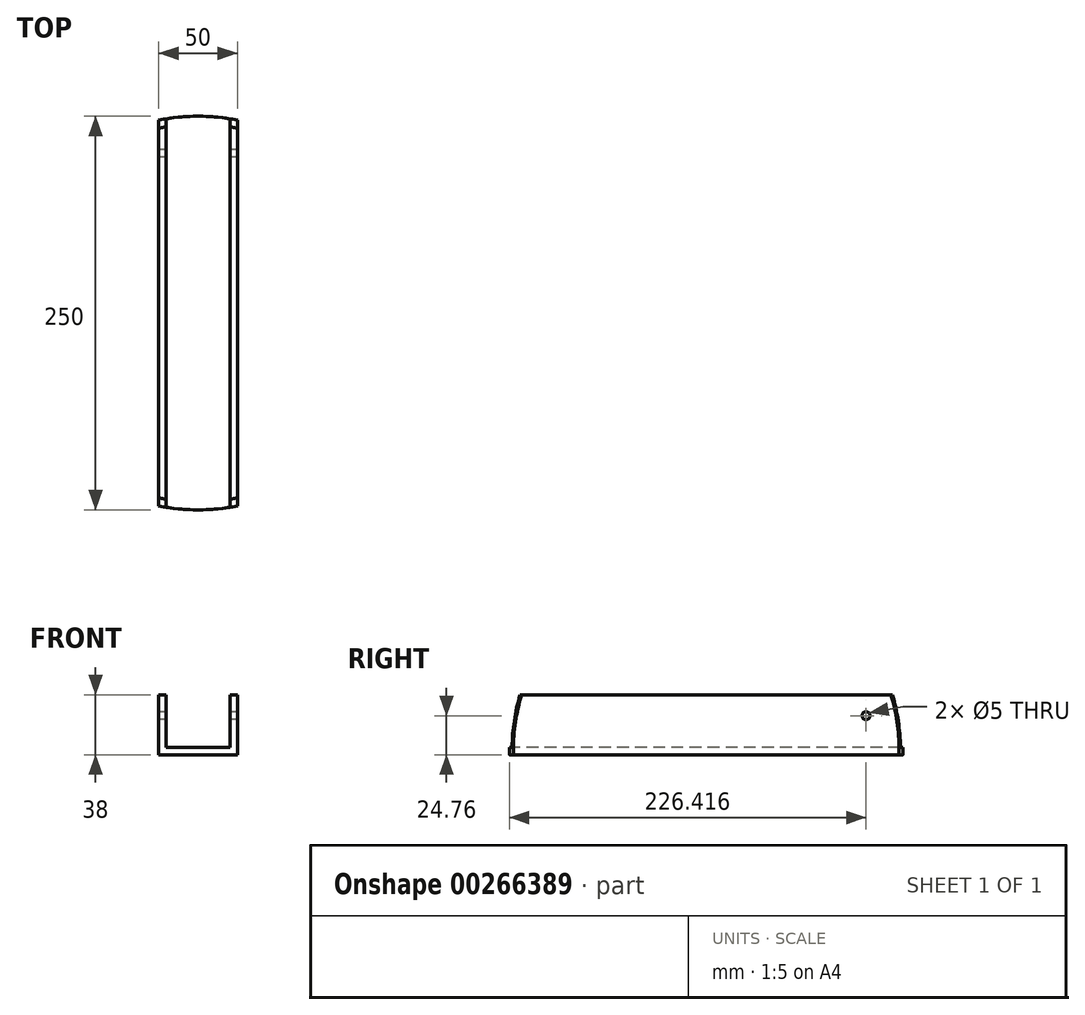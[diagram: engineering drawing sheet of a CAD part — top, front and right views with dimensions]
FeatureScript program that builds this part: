
annotation { "Feature Type Name" : "Feature", "Feature Type Description" : "" }
export const myFeature = defineFeature(function(context is Context, id is Id, definition is map)
    precondition{}
    {
        {
            var Q0;
            Q0=qCreatedBy(makeId("Top.planeOp"),FACE);
            var sketch = newSketch(context, id + "F0", { "sketchPlane" : qUnion([Q0])});
            skCircle(sketch, "E0", {"center": v(0, 0) * mm, "radius": 125 * mm});
            skLineSegment(sketch, "E1", {"start": v(0, 0) * mm, "end": v(0, 125) * mm});
            skLineSegment(sketch, "E2", {"start": v(0, 0) * mm, "end": v(0, -125) * mm});
            skLineSegment(sketch, "E3", {"start": v(0, 0) * mm, "end": v(-25, 0) * mm, "construction": true});
            skLineSegment(sketch, "E4", {"start": v(0, 0) * mm, "end": v(25, 0) * mm, "construction": true});
            skCircle(sketch, "E5", {"center": v(0, 0) * mm, "radius": 122 * mm});
            skLineSegment(sketch, "E6", {"start": v(-25, 90.35) * mm, "end": v(-25, 119.41) * mm});
            skLineSegment(sketch, "E7", {"start": v(25, 90.35) * mm, "end": v(25, 119.41) * mm});
            skLineSegment(sketch, "E8", {"start": v(-25, 119.41) * mm, "end": v(-25, 122.47) * mm});
            skLineSegment(sketch, "E9", {"start": v(25, 119.41) * mm, "end": v(25, 122.47) * mm});
            skLineSegment(sketch, "E10.bottom", {"start": v(3.5, 101.85) * mm, "end": v(-3.5, 101.85) * mm});
            skLineSegment(sketch, "E10.top", {"start": v(3.5, 108.85) * mm, "end": v(-3.5, 108.85) * mm});
            skLineSegment(sketch, "E10.left", {"start": v(3.5, 101.85) * mm, "end": v(3.5, 108.85) * mm});
            skLineSegment(sketch, "E10.right", {"start": v(-3.5, 101.85) * mm, "end": v(-3.5, 108.85) * mm});
            skPoint(sketch, "E10.middle", {"position": v(0, 105.35) * mm});
            skLineSegment(sketch, "E11", {"start": v(-25, 122.47) * mm, "end": v(-25, 125) * mm, "construction": true});
            skLineSegment(sketch, "E12", {"start": v(-25, 125) * mm, "end": v(25, 125) * mm, "construction": true});
            skLineSegment(sketch, "E13", {"start": v(25, 125) * mm, "end": v(25, 122.47) * mm, "construction": true});
            skLineSegment(sketch, "E14", {"start": v(-25, 90.35) * mm, "end": v(-25, 125) * mm, "construction": true});
            skLineSegment(sketch, "E15", {"start": v(-25, 90.35) * mm, "end": v(-25, -119.41) * mm});
            skLineSegment(sketch, "E16", {"start": v(25, 90.35) * mm, "end": v(25, -119.41) * mm});
            skLineSegment(sketch, "E17", {"start": v(-25, 107.67) * mm, "end": v(-20.24, 107.67) * mm, "construction": true});
            skPoint(sketch, "E17.endSnap0", {"position": v(-25, 107.67) * mm});
            skLineSegment(sketch, "E18", {"start": v(-20.24, 107.67) * mm, "end": v(-20.24, 123.35) * mm});
            skLineSegment(sketch, "E19", {"start": v(-20.24, 107.67) * mm, "end": v(-20.24, -120.3) * mm});
            skLineSegment(sketch, "E20", {"start": v(-25, 90.35) * mm, "end": v(-20.24, 90.35) * mm});
            skLineSegment(sketch, "E21", {"start": v(25, 105.35) * mm, "end": v(20.24, 105.35) * mm, "construction": true});
            skLineSegment(sketch, "E22", {"start": v(20.24, 105.35) * mm, "end": v(20.24, 123.35) * mm});
            skLineSegment(sketch, "E23", {"start": v(20.24, 105.35) * mm, "end": v(20.24, -120.3) * mm});
            skLineSegment(sketch, "E24", {"start": v(25, 90.35) * mm, "end": v(20.24, 90.35) * mm});
            skSolve(sketch);
        }
        {
            var Q0;
            {var subQ1=sQuery(id+"F0.wireOp",EDGE,"E1");var subQ3=sQuery(id+"F0.wireOp",EDGE,"E5");var subQ4=makeQuery(id+"F0.imprint","INTERSECT",VERTEX,{"derivedFrom":[subQ1,subQ3]});Q0=makeQuery(id+"F0.imprint","IMPRINT",FACE,{"disambiguationData":[TD([[makeQuery(id+"F0.imprint","IMPRINT",EDGE,{"disambiguationData":[TD([[subQ4,-1.0]])],"derivedFrom":subQ3}),1.0]])]});}
            var Q1;
            {var subQ1=sQuery(id+"F0.wireOp",EDGE,"E1");var subQ3=sQuery(id+"F0.wireOp",EDGE,"E5");var subQ4=makeQuery(id+"F0.imprint","INTERSECT",VERTEX,{"derivedFrom":[subQ1,subQ3]});Q1=makeQuery(id+"F0.imprint","IMPRINT",FACE,{"disambiguationData":[TD([[makeQuery(id+"F0.imprint","IMPRINT",EDGE,{"disambiguationData":[TD([[subQ4,1.0]])],"derivedFrom":subQ3}),1.0]])]});}
            var Q2;
            {var subQ1=sQuery(id+"F0.wireOp",EDGE,"E2");var subQ3=sQuery(id+"F0.wireOp",EDGE,"E5");var subQ4=makeQuery(id+"F0.imprint","INTERSECT",VERTEX,{"derivedFrom":[subQ1,subQ3]});Q2=makeQuery(id+"F0.imprint","IMPRINT",FACE,{"disambiguationData":[TD([[makeQuery(id+"F0.imprint","IMPRINT",EDGE,{"disambiguationData":[TD([[subQ4,1.0]])],"derivedFrom":subQ3}),1.0]])]});}
            var Q3;
            {var subQ1=sQuery(id+"F0.wireOp",EDGE,"E2");var subQ3=sQuery(id+"F0.wireOp",EDGE,"E5");var subQ4=makeQuery(id+"F0.imprint","INTERSECT",VERTEX,{"derivedFrom":[subQ1,subQ3]});Q3=makeQuery(id+"F0.imprint","IMPRINT",FACE,{"disambiguationData":[TD([[makeQuery(id+"F0.imprint","IMPRINT",EDGE,{"disambiguationData":[TD([[subQ4,-1.0]])],"derivedFrom":subQ3}),1.0]])]});}
            var Q4;
            {var subQ0=sQuery(id+"F0.wireOp",EDGE,"7Jiosj1C-cHYn-OFKo-exCg-pKqIQXpvf7Vk");var subQ1=sQuery(id+"F0.wireOp",EDGE,"E0");var subQ2=makeQuery(id+"F0.imprint","INTERSECT",VERTEX,{"derivedFrom":[subQ1,subQ0]});Q4=makeQuery(id+"F0.imprint","IMPRINT",FACE,{"disambiguationData":[TD([[makeQuery(id+"F0.imprint","IMPRINT",EDGE,{"disambiguationData":[TD([[subQ2,-1.0]])],"derivedFrom":subQ1}),1.0]])]});}
            var Q5;
            {var subQ0=sQuery(id+"F0.wireOp",EDGE,"7Jiosj1C-cHYn-OFKo-exCg-pKqIQXpvf7Vk");var subQ1=sQuery(id+"F0.wireOp",EDGE,"E0");var subQ2=makeQuery(id+"F0.imprint","INTERSECT",VERTEX,{"derivedFrom":[subQ1,subQ0]});Q5=makeQuery(id+"F0.imprint","IMPRINT",FACE,{"disambiguationData":[TD([[makeQuery(id+"F0.imprint","IMPRINT",EDGE,{"disambiguationData":[TD([[subQ2,1.0]])],"derivedFrom":subQ1}),1.0]])]});}
            var Q6;
            {var subQ0=sQuery(id+"F0.wireOp",EDGE,"CVOTX2fz-E4fW-4Zke-Np0r-pAHPbpxmWz73");var subQ1=sQuery(id+"F0.wireOp",EDGE,"E0");var subQ2=makeQuery(id+"F0.imprint","INTERSECT",VERTEX,{"derivedFrom":[subQ1,subQ0]});Q6=makeQuery(id+"F0.imprint","IMPRINT",FACE,{"disambiguationData":[TD([[makeQuery(id+"F0.imprint","IMPRINT",EDGE,{"disambiguationData":[TD([[subQ2,-1.0]])],"derivedFrom":subQ1}),1.0]])]});}
            var Q7;
            {var subQ0=sQuery(id+"F0.wireOp",EDGE,"CVOTX2fz-E4fW-4Zke-Np0r-pAHPbpxmWz73");var subQ1=sQuery(id+"F0.wireOp",EDGE,"E0");var subQ2=makeQuery(id+"F0.imprint","INTERSECT",VERTEX,{"derivedFrom":[subQ1,subQ0]});Q7=makeQuery(id+"F0.imprint","IMPRINT",FACE,{"disambiguationData":[TD([[makeQuery(id+"F0.imprint","IMPRINT",EDGE,{"disambiguationData":[TD([[subQ2,1.0]])],"derivedFrom":subQ1}),1.0]])]});}
            var Q8;
            {var subQ0=sQuery(id+"F0.wireOp",EDGE,"lPODcUh7-J9QK-gOea-x6hK-aZiZ33DfVgMm");var subQ1=sQuery(id+"F0.wireOp",EDGE,"E0");var subQ2=makeQuery(id+"F0.imprint","INTERSECT",VERTEX,{"derivedFrom":[subQ1,subQ0]});Q8=makeQuery(id+"F0.imprint","IMPRINT",FACE,{"disambiguationData":[TD([[makeQuery(id+"F0.imprint","IMPRINT",EDGE,{"disambiguationData":[TD([[subQ2,-1.0]])],"derivedFrom":subQ1}),1.0]])]});}
            var Q9;
            {var subQ0=sQuery(id+"F0.wireOp",EDGE,"b5gtcg5E-MX6g-5EKf-npTa-H6z1SQKjBjwp");var subQ1=sQuery(id+"F0.wireOp",EDGE,"E0");var subQ2=makeQuery(id+"F0.imprint","INTERSECT",VERTEX,{"derivedFrom":[subQ1,subQ0]});Q9=makeQuery(id+"F0.imprint","IMPRINT",FACE,{"disambiguationData":[TD([[makeQuery(id+"F0.imprint","IMPRINT",EDGE,{"disambiguationData":[TD([[subQ2,1.0]])],"derivedFrom":subQ1}),1.0]])]});}
            var Q10;
            {var subQ1=sQuery(id+"F0.wireOp",EDGE,"E0");var subQ3=sQuery(id+"F0.wireOp",EDGE,"b5gtcg5E-MX6g-5EKf-npTa-H6z1SQKjBjwp");var subQ4=makeQuery(id+"F0.imprint","INTERSECT",VERTEX,{"derivedFrom":[subQ1,subQ3]});Q10=makeQuery(id+"F0.imprint","IMPRINT",FACE,{"disambiguationData":[TD([[makeQuery(id+"F0.imprint","IMPRINT",EDGE,{"disambiguationData":[TD([[subQ4,1.0]])],"derivedFrom":subQ3}),1.0]])]});}
            var Q11;
            {var subQ1=sQuery(id+"F0.wireOp",EDGE,"E0");var subQ3=sQuery(id+"F0.wireOp",EDGE,"lPODcUh7-J9QK-gOea-x6hK-aZiZ33DfVgMm");var subQ4=makeQuery(id+"F0.imprint","INTERSECT",VERTEX,{"derivedFrom":[subQ1,subQ3]});Q11=makeQuery(id+"F0.imprint","IMPRINT",FACE,{"disambiguationData":[TD([[makeQuery(id+"F0.imprint","IMPRINT",EDGE,{"disambiguationData":[TD([[subQ4,1.0]])],"derivedFrom":subQ3}),-1.0]])]});}
            var Q12;
            {var subQ0=sQuery(id+"F0.wireOp",EDGE,"6XaqNUM2-mYIu-8HfZ-xTXo-2tNdxqEwQb18");var subQ1=sQuery(id+"F0.wireOp",EDGE,"E0");var subQ2=makeQuery(id+"F0.imprint","INTERSECT",VERTEX,{"derivedFrom":[subQ1,subQ0]});Q12=makeQuery(id+"F0.imprint","IMPRINT",FACE,{"disambiguationData":[TD([[makeQuery(id+"F0.imprint","IMPRINT",EDGE,{"disambiguationData":[TD([[subQ2,-1.0]])],"derivedFrom":subQ1}),1.0]])]});}
            var Q13;
            {var subQ1=sQuery(id+"F0.wireOp",EDGE,"E0");var subQ3=sQuery(id+"F0.wireOp",EDGE,"6XaqNUM2-mYIu-8HfZ-xTXo-2tNdxqEwQb18");var subQ4=makeQuery(id+"F0.imprint","INTERSECT",VERTEX,{"derivedFrom":[subQ1,subQ3]});Q13=makeQuery(id+"F0.imprint","IMPRINT",FACE,{"disambiguationData":[TD([[makeQuery(id+"F0.imprint","IMPRINT",EDGE,{"disambiguationData":[TD([[subQ4,-1.0]])],"derivedFrom":subQ3}),1.0]])]});}
            var Q14;
            {var subQ1=sQuery(id+"F0.wireOp",EDGE,"E0");var subQ3=sQuery(id+"F0.wireOp",EDGE,"jOHtUufY-5Agc-4nSS-fDRW-ItwtyQZZNBri");var subQ4=makeQuery(id+"F0.imprint","INTERSECT",VERTEX,{"derivedFrom":[subQ1,subQ3]});Q14=makeQuery(id+"F0.imprint","IMPRINT",FACE,{"disambiguationData":[TD([[makeQuery(id+"F0.imprint","IMPRINT",EDGE,{"disambiguationData":[TD([[subQ4,1.0]])],"derivedFrom":subQ3}),1.0]])]});}
            var Q15;
            {var subQ0=sQuery(id+"F0.wireOp",EDGE,"jOHtUufY-5Agc-4nSS-fDRW-ItwtyQZZNBri");var subQ1=sQuery(id+"F0.wireOp",EDGE,"E0");var subQ2=makeQuery(id+"F0.imprint","INTERSECT",VERTEX,{"derivedFrom":[subQ1,subQ0]});Q15=makeQuery(id+"F0.imprint","IMPRINT",FACE,{"disambiguationData":[TD([[makeQuery(id+"F0.imprint","IMPRINT",EDGE,{"disambiguationData":[TD([[subQ2,1.0]])],"derivedFrom":subQ1}),1.0]])]});}
            var Q16;
            {var subQ0=sQuery(id+"F0.wireOp",EDGE,"E6");Q16=makeQuery(id+"F0.imprint","IMPRINT",FACE,{"disambiguationData":[TD([[makeQuery(id+"F0.imprint","IMPRINT",EDGE,{"derivedFrom":subQ0}),-1.0]])]});}
            var Q17;
            {var subQ5=sQuery(id+"F0.wireOp",EDGE,"E7");Q17=makeQuery(id+"F0.imprint","IMPRINT",FACE,{"disambiguationData":[TD([[makeQuery(id+"F0.imprint","IMPRINT",EDGE,{"derivedFrom":subQ5}),1.0]])]});}
            var Q18;
            {var subQ5=sQuery(id+"F0.wireOp",EDGE,"e795L2u0-bure-mr6k-qCMG-iGtfywM8iEpi");Q18=makeQuery(id+"F0.imprint","IMPRINT",FACE,{"disambiguationData":[TD([[makeQuery(id+"F0.imprint","IMPRINT",EDGE,{"derivedFrom":subQ5}),1.0]])]});}
            var Q19;
            {var subQ5=sQuery(id+"F0.wireOp",EDGE,"pjQDnLFc-Mlye-eH2V-L0hK-29udOUVzYxrg");Q19=makeQuery(id+"F0.imprint","IMPRINT",FACE,{"disambiguationData":[TD([[makeQuery(id+"F0.imprint","IMPRINT",EDGE,{"derivedFrom":subQ5}),-1.0]])]});}
            var Q20;
            {var subQ3=sQuery(id+"F0.wireOp",EDGE,"E15");Q20=makeQuery(id+"F0.imprint","IMPRINT",FACE,{"disambiguationData":[TD([[makeQuery(id+"F0.imprint","IMPRINT",EDGE,{"derivedFrom":subQ3}),1.0]])]});}
            var Q21;
            {var subQ0=sQuery(id+"F0.wireOp",EDGE,"vBihi6ji-Ra4e-OBOK-c5Fv-C3KnZcn3yAMR");Q21=makeQuery(id+"F0.imprint","IMPRINT",FACE,{"disambiguationData":[TD([[makeQuery(id+"F0.imprint","IMPRINT",EDGE,{"derivedFrom":subQ0}),-1.0]])]});}
            var Q22;
            {var subQ3=sQuery(id+"F0.wireOp",EDGE,"E16");Q22=makeQuery(id+"F0.imprint","IMPRINT",FACE,{"disambiguationData":[TD([[makeQuery(id+"F0.imprint","IMPRINT",EDGE,{"derivedFrom":subQ3}),-1.0]])]});}
            var Q23;
            {var subQ0=sQuery(id+"F0.wireOp",EDGE,"kNzFz1E2-5MH9-VqfH-ixdb-lxg0DsbfhWoW");Q23=makeQuery(id+"F0.imprint","IMPRINT",FACE,{"disambiguationData":[TD([[makeQuery(id+"F0.imprint","IMPRINT",EDGE,{"derivedFrom":subQ0}),1.0]])]});}
            extrude(context, id + "F1", {"entities" : qUnion([Q0, Q1, Q2, Q3, Q4, Q5, Q6, Q7, Q8, Q9, Q10, Q11, Q12, Q13, Q14, Q15, Q16, Q17, Q18, Q19, Q20, Q21, Q22, Q23]), "depth" : 4.76 * mm, "offsetDistance" : 25 * mm});
        }
        {
            var Q0;
            Q0=qCreatedBy(makeId("Front.planeOp"),FACE);
            var sketch = newSketch(context, id + "F2", { "sketchPlane" : qUnion([Q0])});
            skCircle(sketch, "E25", {"center": v(0, 3) * mm, "radius": 125 * mm});
            skCircle(sketch, "E26", {"center": v(0, 3) * mm, "radius": 122.5 * mm});
            skLineSegment(sketch, "E27", {"start": v(-125, 3) * mm, "end": v(-122.5, 3) * mm});
            skLineSegment(sketch, "E28", {"start": v(125, 3) * mm, "end": v(122.5, 3) * mm});
            skLineSegment(sketch, "E29", {"start": v(0, 0) * mm, "end": v(0, 128) * mm});
            skCircle(sketch, "E30", {"center": v(0, 3) * mm, "radius": 150 * mm});
            skLineSegment(sketch, "E31", {"start": v(0, 0) * mm, "end": v(0, 153) * mm});
            skLineSegment(sketch, "E32", {"start": v(0, 3) * mm, "end": v(150, 3) * mm});
            skSolve(sketch);
        }
        {
            var Q0;
            Q0=qCreatedBy(makeId("Front.planeOp"),FACE);
            var sketch = newSketch(context, id + "F3", { "sketchPlane" : qUnion([Q0])});
            skCircle(sketch, "E33", {"center": v(0, 3) * mm, "radius": 125 * mm});
            skCircle(sketch, "E34", {"center": v(0, 3) * mm, "radius": 122.5 * mm});
            skLineSegment(sketch, "E35", {"start": v(122.5, 3) * mm, "end": v(125, 3) * mm});
            skLineSegment(sketch, "E36", {"start": v(-122.5, 3) * mm, "end": v(-125, 3) * mm});
            skLineSegment(sketch, "E37", {"start": v(0, 0) * mm, "end": v(0, 128) * mm});
            skSolve(sketch);
        }
        {
            var Q0;
            {var subQ0=sQuery(id+"F0.wireOp",EDGE,"E8");Q0=makeQuery(id+"F0.imprint","IMPRINT",FACE,{"disambiguationData":[TD([[makeQuery(id+"F0.imprint","IMPRINT",EDGE,{"derivedFrom":subQ0}),-1.0]])]});}
            var Q1;
            {var subQ0=sQuery(id+"F0.wireOp",EDGE,"E6");Q1=makeQuery(id+"F0.imprint","IMPRINT",FACE,{"disambiguationData":[TD([[makeQuery(id+"F0.imprint","IMPRINT",EDGE,{"derivedFrom":subQ0}),-1.0]])]});}
            var Q2;
            {var subQ5=sQuery(id+"F0.wireOp",EDGE,"E7");Q2=makeQuery(id+"F0.imprint","IMPRINT",FACE,{"disambiguationData":[TD([[makeQuery(id+"F0.imprint","IMPRINT",EDGE,{"derivedFrom":subQ5}),1.0]])]});}
            var Q3;
            {var subQ0=sQuery(id+"F0.wireOp",EDGE,"E9");Q3=makeQuery(id+"F0.imprint","IMPRINT",FACE,{"disambiguationData":[TD([[makeQuery(id+"F0.imprint","IMPRINT",EDGE,{"derivedFrom":subQ0}),1.0]])]});}
            var Q4;
            {var subQ0=sQuery(id+"F0.wireOp",EDGE,"E16");Q4=makeQuery(id+"F0.imprint","IMPRINT",FACE,{"disambiguationData":[TD([[makeQuery(id+"F0.imprint","IMPRINT",EDGE,{"derivedFrom":subQ0}),-1.0]])]});}
            var Q5;
            {var subQ0=sQuery(id+"F0.wireOp",EDGE,"E15");Q5=makeQuery(id+"F0.imprint","IMPRINT",FACE,{"disambiguationData":[TD([[makeQuery(id+"F0.imprint","IMPRINT",EDGE,{"derivedFrom":subQ0}),1.0]])]});}
            extrude(context, id + "F4", {"entities" : qUnion([Q0, Q1, Q2, Q3, Q4, Q5]), "operationType" : NewBodyOperationType.ADD, "depth" : 38 * mm, "offsetDistance" : 25 * mm});
        }
        {
            var Q0;
            Q0=qCreatedBy(makeId("Right.planeOp"),FACE);
            cPlane(context, id + "F5", {"entities" : qUnion([Q0]), "cplaneType" : CPlaneType.OFFSET, "offset" : 26.6 * mm, "width" : 150 * mm, "height" : 150 * mm});
        }
        {
            var Q0;
            {var subQ0=sQuery(id+"F2.wireOp",EDGE,"E31");var subQ1=sQuery(id+"F2.wireOp",EDGE,"E25");var subQ2=makeQuery(id+"F2.imprint","INTERSECT",VERTEX,{"derivedFrom":[subQ1,subQ0]});Q0=makeQuery(id+"F2.imprint","IMPRINT",FACE,{"disambiguationData":[TD([[makeQuery(id+"F2.imprint","IMPRINT",EDGE,{"disambiguationData":[TD([[subQ2,1.0]])],"derivedFrom":subQ1}),-1.0]])]});}
            var Q1;
            Q1=sQuery(id+"F3.wireOp",EDGE,"E37");
            revolve(context, id + "F6", {"operationType" : NewBodyOperationType.REMOVE, "entities" : qUnion([Q0]), "axis" : qUnion([Q1]), "revolveType" : RevolveType.FULL, "oppositeDirection" : true});
        }
        {
            var Q0;
            Q0=makeQuery(id+"F1.opExtrude","SWEPT_BODY",BODY,{"disambiguationData":[OSD([sQuery(id+"F0.wireOp",EDGE,"E0"),sQuery(id+"F0.wireOp",EDGE,"E5"),sQuery(id+"F0.wireOp",EDGE,"E6"),sQuery(id+"F0.wireOp",EDGE,"E7"),sQuery(id+"F0.wireOp",EDGE,"E8"),sQuery(id+"F0.wireOp",EDGE,"E9"),sQuery(id+"F0.wireOp",EDGE,"E10.bottom"),sQuery(id+"F0.wireOp",EDGE,"E10.top"),sQuery(id+"F0.wireOp",EDGE,"E10.left"),sQuery(id+"F0.wireOp",EDGE,"E10.right"),sQuery(id+"F0.wireOp",EDGE,"E15"),sQuery(id+"F0.wireOp",EDGE,"E16")])]});
            var Q1;
            {var subQ0=sQuery(id+"F2.wireOp",EDGE,"E26");var subQ1=makeQuery(id+"F2.imprint","INTERSECT",VERTEX,{"derivedFrom":[subQ0,sQuery(id+"F2.wireOp",EDGE,"E27")]});Q1=makeQuery(id+"F2.imprint","IMPRINT",FACE,{"disambiguationData":[TD([[makeQuery(id+"F2.imprint","IMPRINT",EDGE,{"disambiguationData":[TD([[subQ1,1.0]])],"derivedFrom":subQ0}),1.0]])]});}
            mirror(context, id + "F7", {"operationType" : NewBodyOperationType.ADD, "entities" : qUnion([Q0]), "mirrorPlane" : qUnion([Q1])});
        }
        {
            var Q0;
            {var subQ0=makeQuery(id+"F4.opExtrude","SWEPT_FACE",FACE,{"disambiguationData":[OSD([sQuery(id+"F0.wireOp",EDGE,"E22"),sQuery(id+"F0.wireOp",EDGE,"E23")])]});Q0=makeQuery(id+"F7.boolean.opBoolean","MERGE",FACE,{"derivedFrom":[subQ0,makeQuery(id+"F7.opPattern","COPY",FACE,{"derivedFrom":subQ0,"instanceName":"1"})]});}
            var sketch = newSketch(context, id + "F8", { "sketchPlane" : qUnion([Q0])});
            skLineSegment(sketch, "E38", {"start": v(-101.42, 4.76) * mm, "end": v(-101.42, 24.76) * mm, "construction": true});
            skCircle(sketch, "E39", {"center": v(-101.42, 24.76) * mm, "radius": 2.5 * mm});
            skLineSegment(sketch, "E40", {"start": v(-101.42, 24.76) * mm, "end": v(-121.42, 24.76) * mm, "construction": true});
            skSolve(sketch);
        }
        {
            var Q0;
            Q0=makeQuery(id+"F8.imprint","IMPRINT",FACE,{"disambiguationData":[TD([[makeQuery(id+"F8.imprint","IMPRINT",EDGE,{"derivedFrom":sQuery(id+"F8.wireOp",EDGE,"E39")}),1.0]])]});
            extrude(context, id + "F9", {"entities" : qUnion([Q0]), "operationType" : NewBodyOperationType.REMOVE, "endBound" : BoundingType.THROUGH_ALL, "oppositeDirection" : true, "depth" : 25 * mm, "offsetDistance" : 25 * mm, "hasSecondDirection" : true, "secondDirectionBound" : SecondDirectionBoundingType.THROUGH_ALL, "secondDirectionOppositeDirection" : false, "secondDirectionDepth" : 25 * mm});
        }
    });
